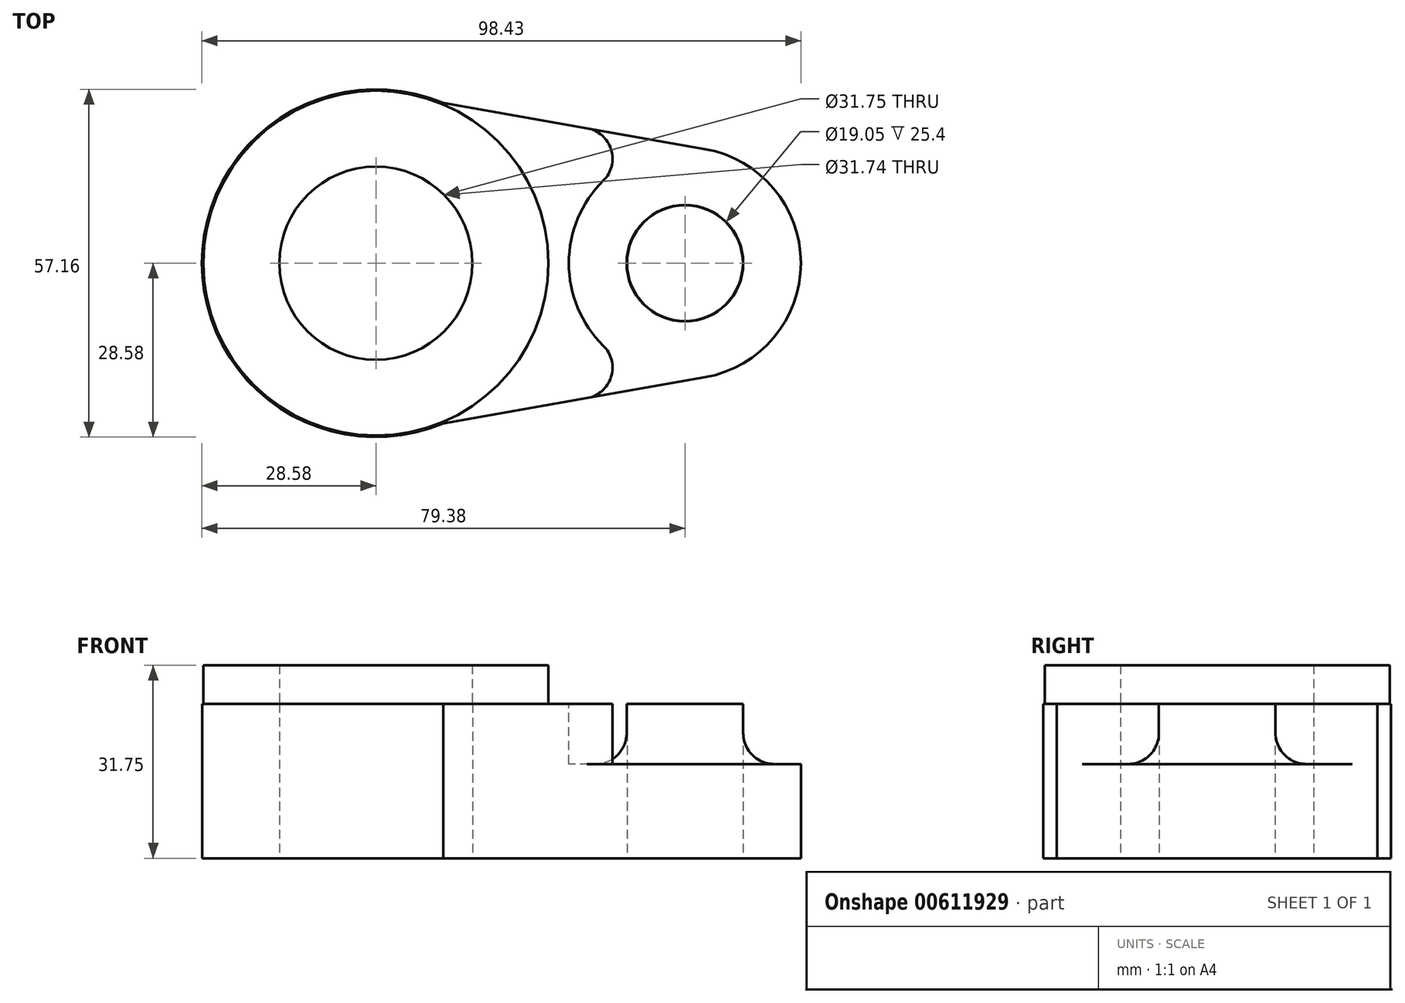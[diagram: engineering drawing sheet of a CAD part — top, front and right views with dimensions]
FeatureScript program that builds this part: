
annotation { "Feature Type Name" : "Feature", "Feature Type Description" : "" }
export const myFeature = defineFeature(function(context is Context, id is Id, definition is map)
    precondition{}
    {
        {
            var Q0;
            Q0=qCreatedBy(makeId("Top.planeOp"),FACE);
            var sketch = newSketch(context, id + "F0", { "sketchPlane" : qUnion([Q0])});
            skCircle(sketch, "E0", {"center": v(0, 0) * mm, "radius": 15.88 * mm});
            skCircle(sketch, "E1", {"center": v(0, 0) * mm, "radius": 28.58 * mm});
            skCircle(sketch, "E2", {"center": v(50.8, 0) * mm, "radius": 9.53 * mm});
            skCircle(sketch, "E3", {"center": v(50.8, 0) * mm, "radius": 19.05 * mm});
            skLineSegment(sketch, "E4", {"start": v(11.06, 26.35) * mm, "end": v(54.1, 18.76) * mm});
            skLineSegment(sketch, "E5", {"start": v(54.1, -18.76) * mm, "end": v(11.06, -26.35) * mm});
            skSolve(sketch);
        }
        {
            var Q0;
            Q0 = qSketchRegion(id + "F0", true);
            extrude(context, id + "F1", {"entities" : qUnion([Q0]), "depth" : 25.4 * mm, "offsetDistance" : 25.4 * mm});
        }
        {
            var Q0;
            Q0=qCreatedBy(makeId("Top.planeOp"),FACE);
            var sketch = newSketch(context, id + "F2", { "sketchPlane" : qUnion([Q0])});
            skCircle(sketch, "E6", {"center": v(0, 0) * mm, "radius": 28.35 * mm});
            skCircle(sketch, "E7", {"center": v(0, 0) * mm, "radius": 15.87 * mm});
            skSolve(sketch);
        }
        {
            var Q0;
            Q0 = qSketchRegion(id + "F2", true);
            extrude(context, id + "F3", {"entities" : qUnion([Q0]), "operationType" : NewBodyOperationType.ADD, "depth" : 31.75 * mm, "offsetDistance" : 25.4 * mm});
        }
        {
            var Q0;
            Q0=makeQuery(id+"F1.opExtrude","CAP_FACE",FACE,{"disambiguationData":[OSD([sQuery(id+"F0.wireOp",EDGE,"E0"),sQuery(id+"F0.wireOp",EDGE,"E1"),sQuery(id+"F0.wireOp",EDGE,"E2"),sQuery(id+"F0.wireOp",EDGE,"E3"),sQuery(id+"F0.wireOp",EDGE,"E4"),sQuery(id+"F0.wireOp",EDGE,"E5")])],"isStart":false});
            var sketch = newSketch(context, id + "F4", { "sketchPlane" : qUnion([Q0])});
            skCircle(sketch, "E8", {"center": v(50.8, 0) * mm, "radius": 9.58 * mm});
            skCircle(sketch, "E9", {"center": v(50.8, 0) * mm, "radius": 19.08 * mm});
            skSolve(sketch);
        }
        {
            var Q0;
            Q0 = qSketchRegion(id + "F4", true);
            extrude(context, id + "F5", {"entities" : qUnion([Q0]), "operationType" : NewBodyOperationType.REMOVE, "oppositeDirection" : true, "depth" : 9.9 * mm, "offsetDistance" : 25.4 * mm});
        }
        {
            var Q0;
            Q0=makeQuery(id+"F5.boolean.opBoolean","INTERSECT",EDGE,{"derivedFrom":[makeQuery(id+"F1.opExtrude","SWEPT_FACE",FACE,{"disambiguationData":[OSD([sQuery(id+"F0.wireOp",EDGE,"E4")])]}),makeQuery(id+"F5.opExtrude","SWEPT_FACE",FACE,{"disambiguationData":[OSD([sQuery(id+"F4.wireOp",EDGE,"E9")])]})]});
            var Q1;
            Q1=makeQuery(id+"F5.boolean.opBoolean","INTERSECT",EDGE,{"derivedFrom":[makeQuery(id+"F1.opExtrude","SWEPT_FACE",FACE,{"disambiguationData":[OSD([sQuery(id+"F0.wireOp",EDGE,"E5")])]}),makeQuery(id+"F5.opExtrude","SWEPT_FACE",FACE,{"disambiguationData":[OSD([sQuery(id+"F4.wireOp",EDGE,"E9")])]})]});
            var Q2;
            Q2=makeQuery(id+"F5.boolean.opBoolean","COPY",EDGE,{"derivedFrom":makeQuery(id+"F5.opExtrude","CAP_EDGE",EDGE,{"disambiguationData":[OSD([sQuery(id+"F4.wireOp",EDGE,"E8")])],"isStart":false})});
            fillet(context, id + "F6", {"entities" : qUnion([Q0, Q1, Q2]), "radius" : 5.08 * mm, "tangentPropagation" : true, "allowEdgeOverflow" : false});
        }
    });
